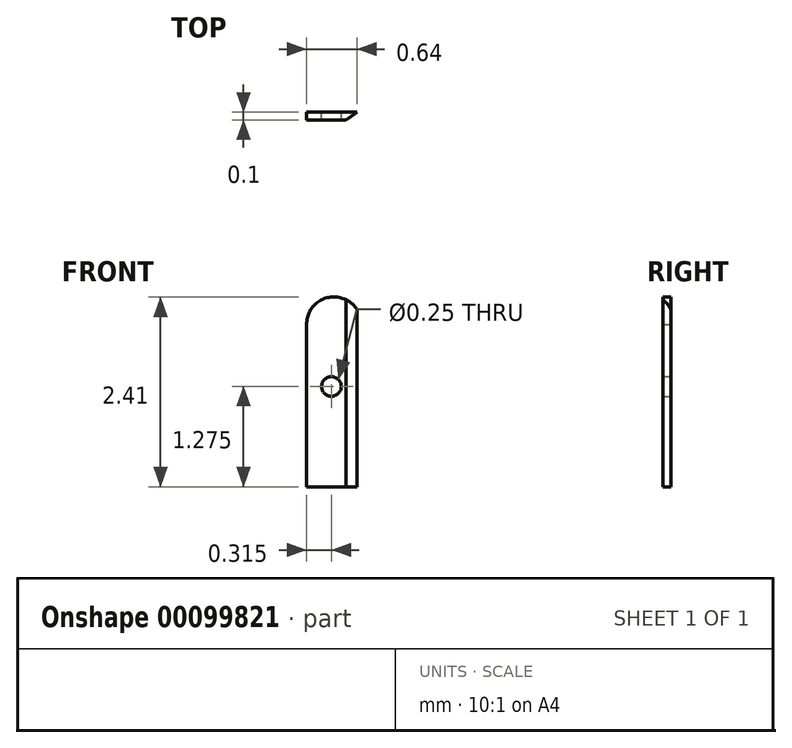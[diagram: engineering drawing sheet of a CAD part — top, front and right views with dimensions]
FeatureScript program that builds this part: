
annotation { "Feature Type Name" : "Feature", "Feature Type Description" : "" }
export const myFeature = defineFeature(function(context is Context, id is Id, definition is map)
    precondition{}
    {
        {
            var Q0;
            Q0=qCreatedBy(makeId("Front.planeOp"),FACE);
            var sketch = newSketch(context, id + "F0", { "sketchPlane" : qUnion([Q0])});
            skLineSegment(sketch, "E0", {"start": v(0, 0) * mm, "end": v(0.5, 0) * mm});
            skLineSegment(sketch, "E1", {"start": v(0.64, 0) * mm, "end": v(0.5, 0) * mm});
            skLineSegment(sketch, "E2", {"start": v(0, 0) * mm, "end": v(0, 2.06) * mm});
            skLineSegment(sketch, "E3", {"start": v(0.25, 0) * mm, "end": v(0.25, 2.4) * mm, "construction": true});
            skLineSegment(sketch, "E4", {"start": v(0.64, 0) * mm, "end": v(0.64, 2.25) * mm});
            skArc(sketch, "E5", {"start": v(0.64, 2.25) * mm, "mid": v(0.25, 2.4) * mm, "end": v(0, 2.06) * mm});
            skLineSegment(sketch, "E6", {"start": v(0.5, 0) * mm, "end": v(0.5, 2.38) * mm});
            skCircle(sketch, "E7", {"center": v(0.32, 1.28) * mm, "radius": 0.12 * mm});
            skSolve(sketch);
        }
        {
            var Q0;
            Q0 = qSketchRegion(id + "F0", true);
            extrude(context, id + "F1", {"entities" : qUnion([Q0]), "depth" : 0.1 * mm});
        }
        {
            var Q0;
            Q0=makeQuery(id+"F1.opExtrude","CAP_EDGE",EDGE,{"disambiguationData":[OSD([sQuery(id+"F0.wireOp",EDGE,"E4")])],"isStart":false});
            chamfer(context, id + "F2", {"entities" : qUnion([Q0]), "chamferType" : ChamferType.TWO_OFFSETS, "width1" : 0.14 * mm, "oppositeDirection" : false, "width2" : 0.1 * mm, "tangentPropagation" : true});
        }
    });
